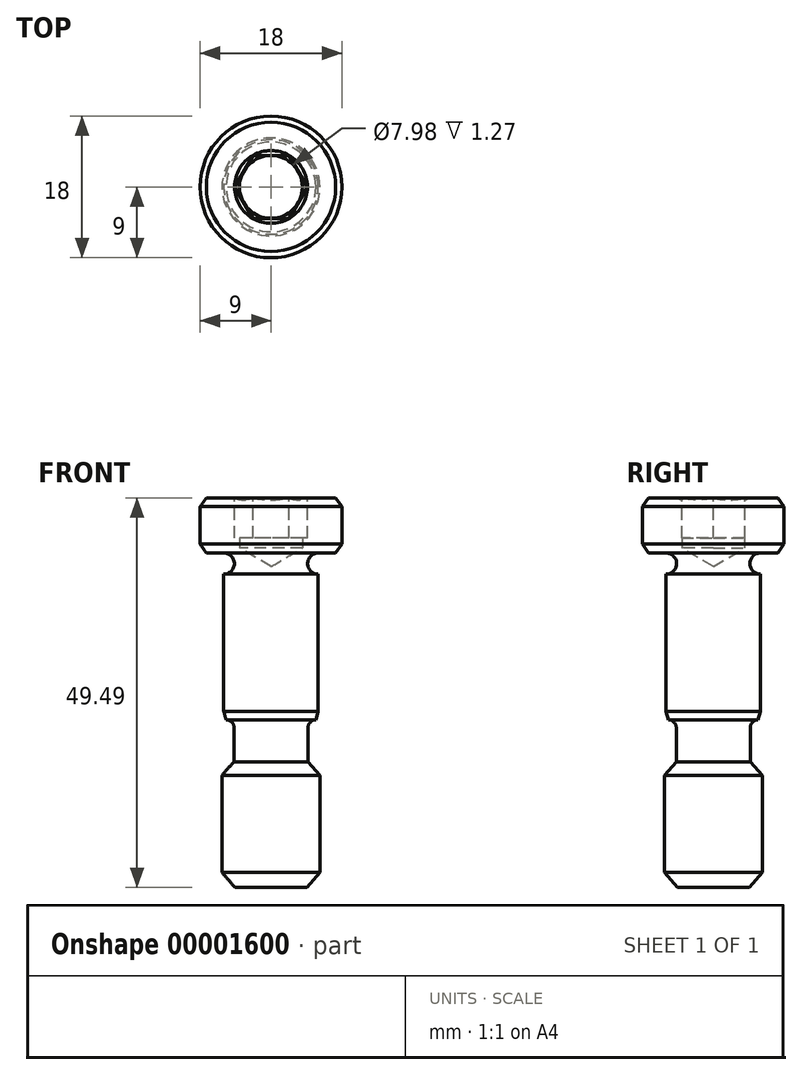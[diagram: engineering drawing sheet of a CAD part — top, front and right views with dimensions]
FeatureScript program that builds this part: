
annotation { "Feature Type Name" : "Feature", "Feature Type Description" : "" }
export const myFeature = defineFeature(function(context is Context, id is Id, definition is map)
    precondition{}
    {
        {
            var Q0;
            Q0=qCreatedBy(makeId("Front.planeOp"),FACE);
            var sketch = newSketch(context, id + "F0", { "sketchPlane" : qUnion([Q0])});
            skLineSegment(sketch, "E0", {"start": v(0, 0) * mm, "end": v(8.21, 0) * mm});
            skLineSegment(sketch, "E1", {"start": v(9, -1.12) * mm, "end": v(9, -5.89) * mm});
            skLineSegment(sketch, "E2", {"start": v(9, -5.89) * mm, "end": v(8.21, -7) * mm});
            skLineSegment(sketch, "E3", {"start": v(8.21, -7) * mm, "end": v(6, -7) * mm});
            skArc(sketch, "E4", {"start": v(6, -7) * mm, "mid": v(4.66, -8.35) * mm, "end": v(6, -9.7) * mm});
            skLineSegment(sketch, "E5", {"start": v(6, -9.7) * mm, "end": v(6, -27.1) * mm});
            skLineSegment(sketch, "E6", {"start": v(6, -27.1) * mm, "end": v(5.7, -28.2) * mm});
            skLineSegment(sketch, "E7", {"start": v(4.7, -29.2) * mm, "end": v(4.7, -33.52) * mm});
            skLineSegment(sketch, "E8", {"start": v(4.7, -33.52) * mm, "end": v(6.23, -35.24) * mm});
            skLineSegment(sketch, "E9", {"start": v(6.23, -35.24) * mm, "end": v(6.23, -47.59) * mm});
            skLineSegment(sketch, "E10", {"start": v(6.23, -47.59) * mm, "end": v(4.57, -49.5) * mm});
            skLineSegment(sketch, "E11", {"start": v(4.57, -49.5) * mm, "end": v(0, -49.5) * mm});
            skLineSegment(sketch, "E12", {"start": v(0, -49.5) * mm, "end": v(0, 0) * mm});
            skLineSegment(sketch, "E13", {"start": v(8.21, 0) * mm, "end": v(9, -1.12) * mm});
            skArc(sketch, "E14", {"start": v(5.7, -28.2) * mm, "mid": v(5, -28.5) * mm, "end": v(4.7, -29.2) * mm});
            skLineSegment(sketch, "E15", {"start": v(3.99, -6.35) * mm, "end": v(0, -8.75) * mm});
            skLineSegment(sketch, "E16", {"start": v(3.99, -6.35) * mm, "end": v(3.99, 0) * mm});
            skSolve(sketch);
        }
        {
            var Q0;
            Q0=makeQuery(id+"F0.imprint","IMPRINT",FACE,{"disambiguationData":[TD([[makeQuery(id+"F0.imprint","IMPRINT",EDGE,{"derivedFrom":sQuery(id+"F0.wireOp",EDGE,"E1")}),-1.0]])]});
            var Q1;
            Q1=sQuery(id+"F0.wireOp",EDGE,"E12");
            revolve(context, id + "F1", {"entities" : qUnion([Q0]), "axis" : qUnion([Q1]), "revolveType" : RevolveType.FULL});
        }
        {
            var Q0;
            Q0=qCreatedBy(makeId("Top.planeOp"),FACE);
            var sketch = newSketch(context, id + "F2", { "sketchPlane" : qUnion([Q0])});
            skCircle(sketch, "E17", {"center": v(0, 0) * mm, "radius": 4.62 * mm, "construction": true});
            skLineSegment(sketch, "E18", {"start": v(-2.3, -4) * mm, "end": v(-4.62, 0) * mm});
            skLineSegment(sketch, "E19", {"start": v(-4.62, 0) * mm, "end": v(-2.3, 4) * mm});
            skLineSegment(sketch, "E20", {"start": v(-2.3, 4) * mm, "end": v(2.3, 4) * mm});
            skLineSegment(sketch, "E21", {"start": v(2.3, 4) * mm, "end": v(4.62, 0) * mm});
            skLineSegment(sketch, "E22", {"start": v(4.62, 0) * mm, "end": v(2.3, -4) * mm});
            skLineSegment(sketch, "E23", {"start": v(2.3, -4) * mm, "end": v(-2.3, -4) * mm});
            skSolve(sketch);
        }
        {
            var Q0;
            Q0=makeQuery(id+"F2.imprint","IMPRINT",FACE,{"disambiguationData":[TD([[makeQuery(id+"F2.imprint","IMPRINT",EDGE,{"derivedFrom":sQuery(id+"F2.wireOp",EDGE,"E18")}),-1.0]])]});
            extrude(context, id + "F3", {"entities" : qUnion([Q0]), "operationType" : NewBodyOperationType.REMOVE, "oppositeDirection" : true, "depth" : 5.08 * mm});
        }
        {
            var Q0;
            Q0=qCreatedBy(makeId("Front.planeOp"),FACE);
            var sketch = newSketch(context, id + "F4", { "sketchPlane" : qUnion([Q0])});
            skPoint(sketch, "E24.0", {"position": v(4.62, 0) * mm});
            skPoint(sketch, "E25.1", {"position": v(-4.62, 0) * mm});
            skArc(sketch, "E26", {"start": v(-4.62, 0) * mm, "mid": v(0, -1) * mm, "end": v(4.62, 0) * mm});
            skLineSegment(sketch, "E27", {"start": v(0, 0) * mm, "end": v(0, -1) * mm});
            skLineSegment(sketch, "E28", {"start": v(-4.62, 0) * mm, "end": v(0, 0) * mm});
            skSolve(sketch);
        }
        {
            var Q0;
            {var subQ1=sQuery(id+"F4.wireOp",EDGE,"E27");Q0=makeQuery(id+"F4.imprint","IMPRINT",FACE,{"disambiguationData":[TD([[makeQuery(id+"F4.imprint","IMPRINT",EDGE,{"derivedFrom":subQ1}),-1.0]])]});}
            var Q1;
            Q1=sQuery(id+"F4.wireOp",EDGE,"E27");
            revolve(context, id + "F5", {"operationType" : NewBodyOperationType.REMOVE, "entities" : qUnion([Q0]), "axis" : qUnion([Q1]), "revolveType" : RevolveType.FULL, "oppositeDirection" : true});
        }
    });
